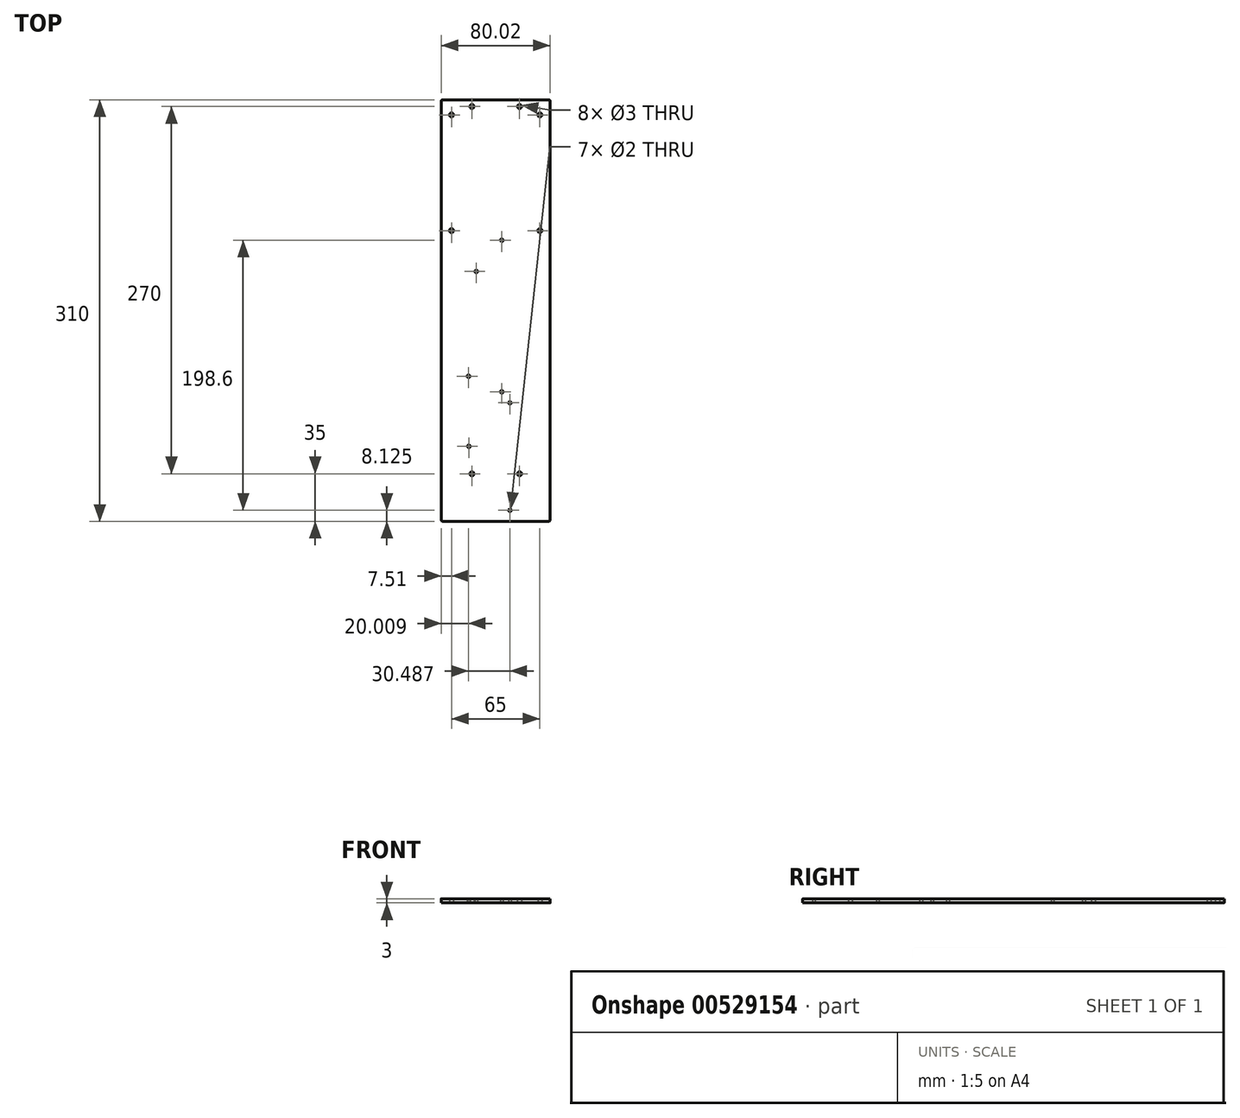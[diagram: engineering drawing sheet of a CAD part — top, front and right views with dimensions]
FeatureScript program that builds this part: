
annotation { "Feature Type Name" : "Feature", "Feature Type Description" : "" }
export const myFeature = defineFeature(function(context is Context, id is Id, definition is map)
    precondition{}
    {
        {
            var Q0;
            Q0=qCreatedBy(makeId("Top.planeOp"),FACE);
            var sketch = newSketch(context, id + "F0", { "sketchPlane" : qUnion([Q0])});
            skLineSegment(sketch, "E0", {"start": v(-17.5, 141.56) * mm, "end": v(-17.5, -144.63) * mm, "construction": true});
            skLineSegment(sketch, "E1", {"start": v(-37.83, 135) * mm, "end": v(37.33, 135) * mm, "construction": true});
            skLineSegment(sketch, "E2", {"start": v(0, 146.02) * mm, "end": v(0, -146.75) * mm, "construction": true});
            skPoint(sketch, "E2.startSnap0", {"position": v(0, 140) * mm});
            skLineSegment(sketch, "E3.MirrorCS", {"start": v(17.5, 141.56) * mm, "end": v(17.5, -144.63) * mm, "construction": true});
            skLineSegment(sketch, "E4", {"start": v(-42.31, 0) * mm, "end": v(45.96, 0) * mm, "construction": true});
            skPoint(sketch, "E4.startSnap0", {"position": v(-32.5, 0) * mm});
            skPoint(sketch, "E4.endSnap0", {"position": v(32.5, 0) * mm});
            skCircle(sketch, "E5", {"center": v(-17.5, 135) * mm, "radius": 1.5 * mm});
            skCircle(sketch, "E6.MirrorC", {"center": v(17.5, 135) * mm, "radius": 1.5 * mm});
            skCircle(sketch, "E7.MirrorC", {"center": v(-17.5, -135) * mm, "radius": 1.5 * mm});
            skCircle(sketch, "E8.MirrorC", {"center": v(17.5, -135) * mm, "radius": 1.5 * mm});
            skLineSegment(sketch, "E9.top", {"start": v(39.01, 140) * mm, "end": v(-39.01, 140) * mm});
            skPoint(sketch, "E9.middle", {"position": v(0, 0) * mm});
            skLineSegment(sketch, "E10", {"start": v(0, 135.95) * mm, "end": v(0, 37.87) * mm, "construction": true});
            skPoint(sketch, "E10.startSnap0", {"position": v(0, 131.8) * mm});
            skLineSegment(sketch, "E11", {"start": v(-38.86, 86.27) * mm, "end": v(39, 86.27) * mm, "construction": true});
            skPoint(sketch, "E11.startSnap0", {"position": v(-35.5, 86.27) * mm});
            skCircle(sketch, "E12", {"center": v(-32.5, 128.8) * mm, "radius": 1.5 * mm});
            skCircle(sketch, "E13.MirrorC", {"center": v(32.5, 128.8) * mm, "radius": 1.5 * mm});
            skCircle(sketch, "E14.MirrorC", {"center": v(-32.5, 43.73) * mm, "radius": 1.5 * mm});
            skCircle(sketch, "E15.MirrorC", {"center": v(32.5, 43.73) * mm, "radius": 1.5 * mm});
            skCircle(sketch, "E16.MirrorC", {"center": v(4.5, 36.73) * mm, "radius": 1 * mm});
            skCircle(sketch, "E17.MirrorC", {"center": v(4.5, -74.77) * mm, "radius": 1 * mm});
            skCircle(sketch, "E18.MirrorC", {"center": v(-20, -63.27) * mm, "radius": 1 * mm});
            skCircle(sketch, "E19.MirrorC", {"center": v(-14.3, 13.73) * mm, "radius": 1 * mm});
            skCircle(sketch, "E20.MirrorC", {"center": v(10.49, -82.87) * mm, "radius": 1 * mm});
            skCircle(sketch, "E21.MirrorC", {"center": v(-19.71, -114.87) * mm, "radius": 1 * mm});
            skPoint(sketch, "E22.oppositeSnap0", {"position": v(40.01, 0) * mm});
            skLineSegment(sketch, "E22.top", {"start": v(-39.01, -170) * mm, "end": v(39.01, -170) * mm});
            skLineSegment(sketch, "E22.left", {"start": v(-40.01, 139) * mm, "end": v(-40.01, -169) * mm});
            skLineSegment(sketch, "E22.right", {"start": v(40.01, 139) * mm, "end": v(40.01, -169) * mm});
            skCircle(sketch, "E23.MirrorC", {"center": v(10.49, -161.87) * mm, "radius": 1 * mm});
            skPoint(sketch, "E24.visualSharp", {"position": v(-40.01, 140) * mm});
            skArc(sketch, "E24.filletArc", {"start": v(-39.01, 140) * mm, "mid": v(-39.72, 139.7) * mm, "end": v(-40.01, 139) * mm});
            skPoint(sketch, "E25.visualSharp", {"position": v(40.01, 140) * mm});
            skArc(sketch, "E25.filletArc", {"start": v(40.01, 139) * mm, "mid": v(39.72, 139.7) * mm, "end": v(39.01, 140) * mm});
            skPoint(sketch, "E26.visualSharp", {"position": v(-40.01, -170) * mm});
            skArc(sketch, "E26.filletArc", {"start": v(-40.01, -169) * mm, "mid": v(-39.72, -169.7) * mm, "end": v(-39.01, -170) * mm});
            skPoint(sketch, "E27.visualSharp", {"position": v(40.01, -170) * mm});
            skArc(sketch, "E27.filletArc", {"start": v(39.01, -170) * mm, "mid": v(39.72, -169.7) * mm, "end": v(40.01, -169) * mm});
            skSolve(sketch);
        }
        {
            var Q0;
            Q0 = qSketchRegion(id + "F0", true);
            extrude(context, id + "F1", {"entities" : qUnion([Q0]), "depth" : 3 * mm, "offsetDistance" : 25 * mm});
        }
    });
